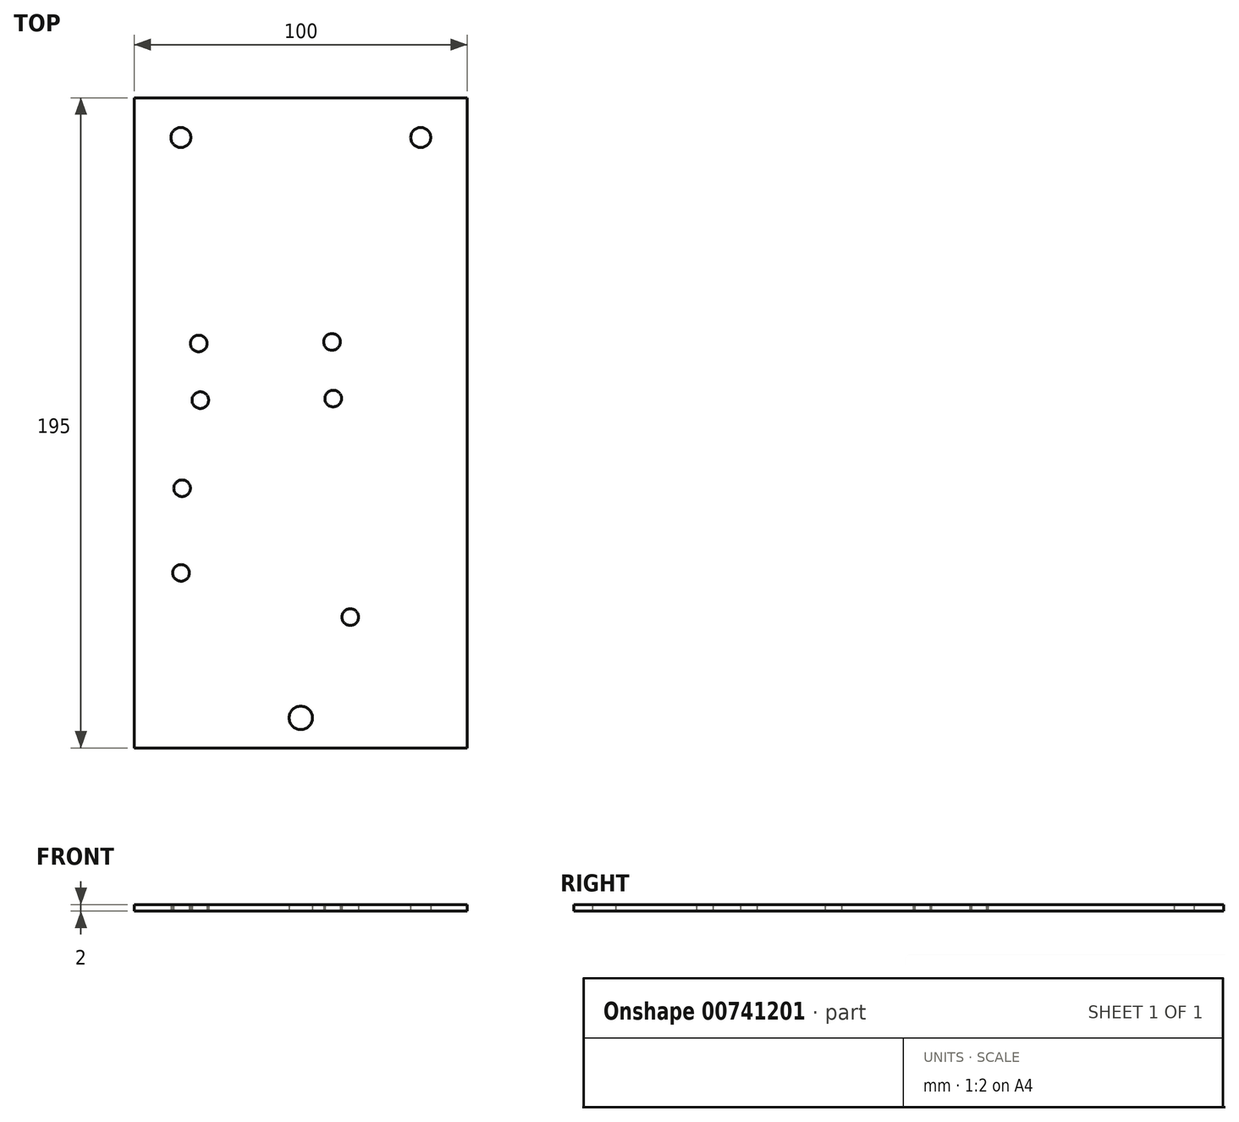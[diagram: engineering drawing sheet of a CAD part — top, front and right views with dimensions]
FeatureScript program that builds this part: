
annotation { "Feature Type Name" : "Feature", "Feature Type Description" : "" }
export const myFeature = defineFeature(function(context is Context, id is Id, definition is map)
    precondition{}
    {
        {
            var Q0;
            Q0=qCreatedBy(makeId("Top.planeOp"),FACE);
            var sketch = newSketch(context, id + "F0", { "sketchPlane" : qUnion([Q0])});
            skLineSegment(sketch, "E0.bottom", {"start": v(0, -3.6) * mm, "end": v(100, -3.6) * mm});
            skLineSegment(sketch, "E0.top", {"start": v(0, 191.4) * mm, "end": v(100, 191.4) * mm});
            skLineSegment(sketch, "E0.left", {"start": v(0, -3.6) * mm, "end": v(0, 191.4) * mm});
            skLineSegment(sketch, "E0.right", {"start": v(100, -3.6) * mm, "end": v(100, 191.4) * mm});
            skLineSegment(sketch, "E1", {"start": v(0, 126.4) * mm, "end": v(100, 126.4) * mm});
            skLineSegment(sketch, "E2", {"start": v(0, 26.4) * mm, "end": v(100, 26.4) * mm});
            skLineSegment(sketch, "E3", {"start": v(50, 191.4) * mm, "end": v(50, 0) * mm, "construction": true});
            skCircle(sketch, "E4", {"center": v(14, 179.53) * mm, "radius": 3 * mm});
            skCircle(sketch, "E5.MirrorC", {"center": v(86, 179.53) * mm, "radius": 3 * mm});
            skCircle(sketch, "E6", {"center": v(50, 5.4) * mm, "radius": 3.5 * mm});
            skCircle(sketch, "E7", {"center": v(14.37, 74.29) * mm, "radius": 2.5 * mm});
            skCircle(sketch, "E8", {"center": v(14.05, 48.9) * mm, "radius": 2.5 * mm});
            skCircle(sketch, "E9", {"center": v(64.85, 35.63) * mm, "radius": 2.5 * mm});
            skCircle(sketch, "E10", {"center": v(19.36, 117.72) * mm, "radius": 2.5 * mm});
            skCircle(sketch, "E11", {"center": v(19.84, 100.72) * mm, "radius": 2.5 * mm});
            skCircle(sketch, "E12", {"center": v(59.36, 118.2) * mm, "radius": 2.5 * mm});
            skCircle(sketch, "E13", {"center": v(59.72, 101.2) * mm, "radius": 2.5 * mm});
            skSolve(sketch);
        }
        {
            var Q0;
            Q0 = qSketchRegion(id + "F0", true);
            extrude(context, id + "F1", {"entities" : qUnion([Q0]), "depth" : 2 * mm, "offsetDistance" : 25 * mm});
        }
    });
